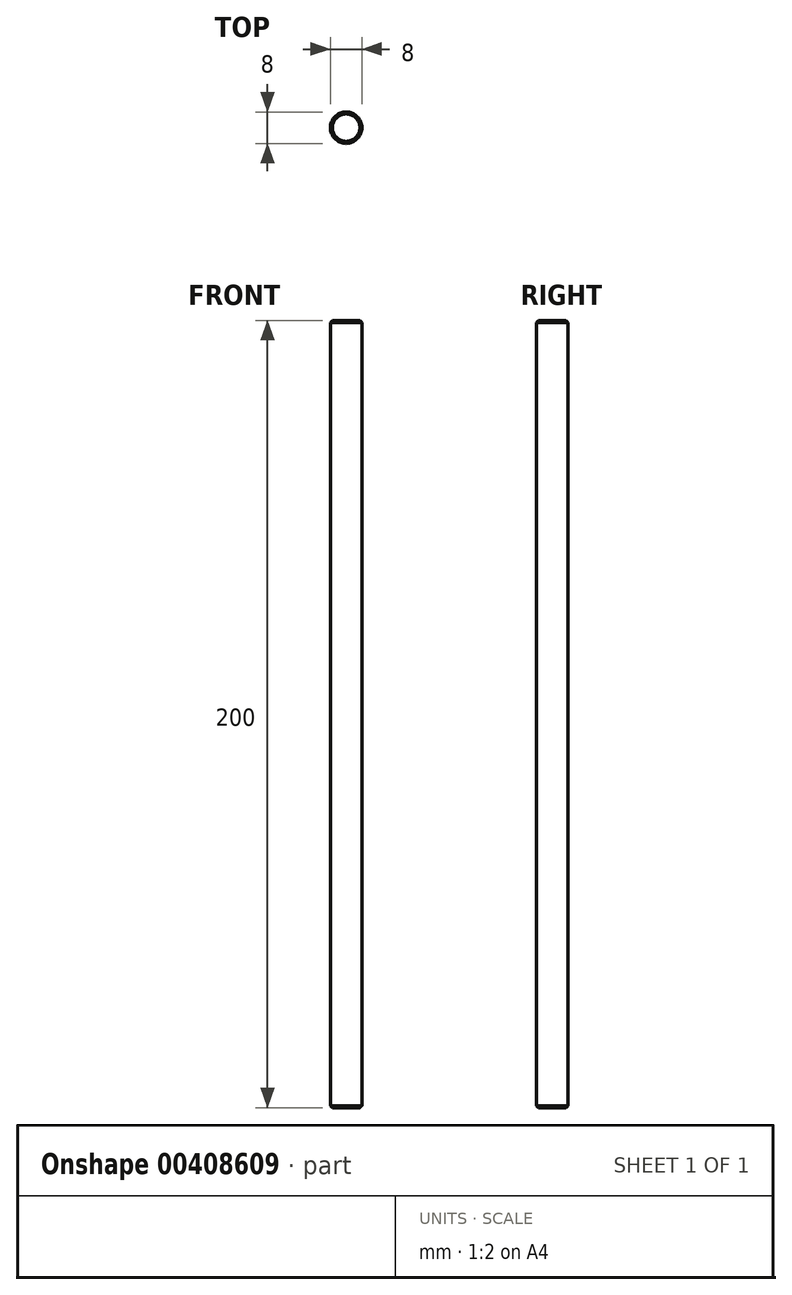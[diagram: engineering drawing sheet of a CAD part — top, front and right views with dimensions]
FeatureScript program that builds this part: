
annotation { "Feature Type Name" : "Feature", "Feature Type Description" : "" }
export const myFeature = defineFeature(function(context is Context, id is Id, definition is map)
    precondition{}
    {
        {
            var Q0;
            Q0=qCreatedBy(makeId("Top.planeOp"),FACE);
            var sketch = newSketch(context, id + "F0", { "sketchPlane" : qUnion([Q0])});
            skCircle(sketch, "E0", {"center": v(0, 0) * mm, "radius": 4 * mm});
            skSolve(sketch);
        }
        {
            var Q0;
            Q0 = qSketchRegion(id + "F0", true);
            extrude(context, id + "F1", {"entities" : qUnion([Q0]), "depth" : 200 * mm});
        }
        {
            var Q0;
            Q0=makeQuery(id+"F1.opExtrude","SWEPT_FACE",FACE,{"disambiguationData":[OSD([sQuery(id+"F0.wireOp",EDGE,"E0")])]});
            chamfer(context, id + "F2", {"entities" : qUnion([Q0]), "width" : .5 * mm, "tangentPropagation" : true});
        }
    });
